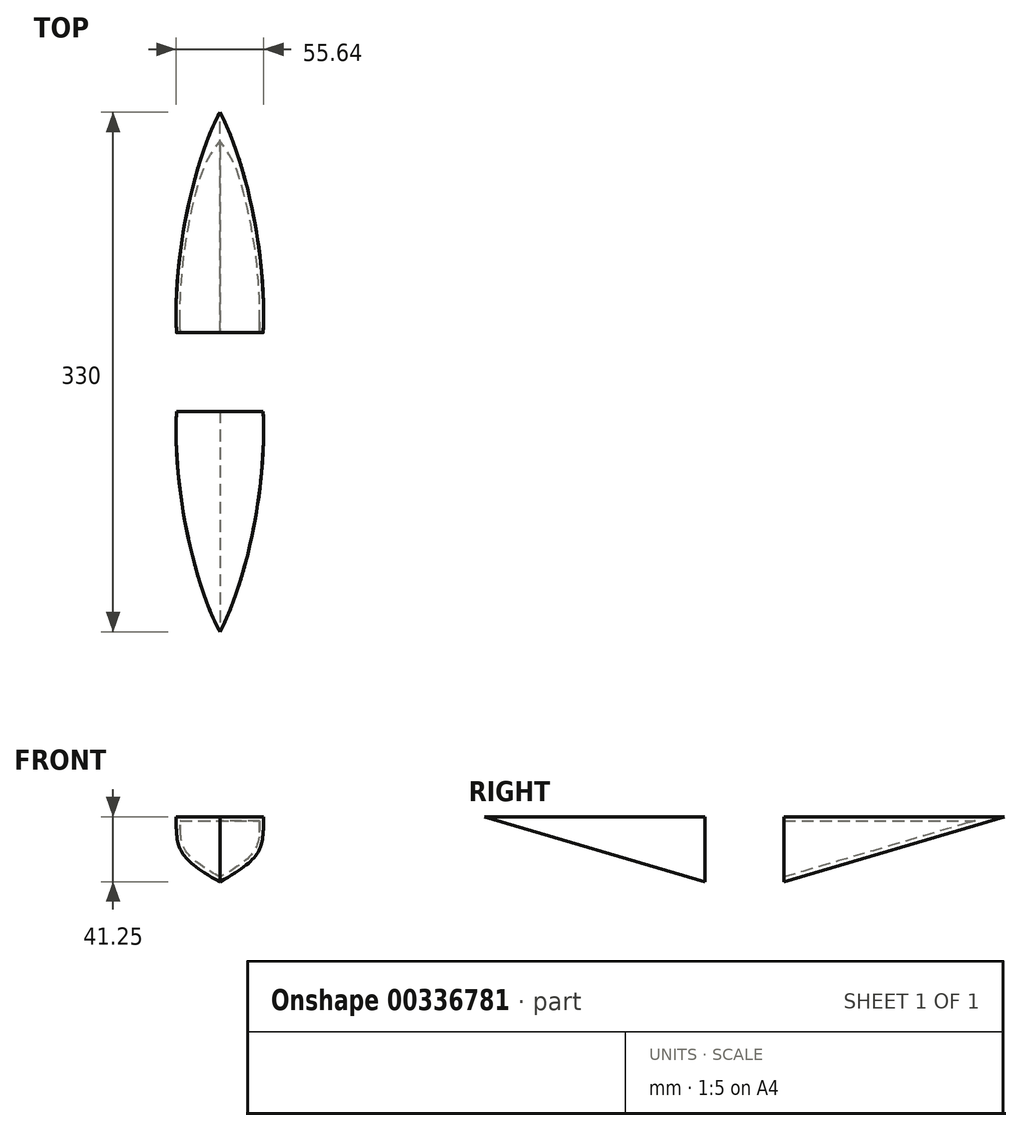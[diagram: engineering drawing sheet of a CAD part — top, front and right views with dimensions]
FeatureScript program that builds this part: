
annotation { "Feature Type Name" : "Feature", "Feature Type Description" : "" }
export const myFeature = defineFeature(function(context is Context, id is Id, definition is map)
    precondition{}
    {
        {
            var Q0;
            Q0=qCreatedBy(makeId("Front.planeOp"),FACE);
            cPlane(context, id + "F0", {"entities" : qUnion([Q0]), "cplaneType" : CPlaneType.OFFSET, "offset" : 25 * mm, "width" : 150 * mm, "height" : 150 * mm});
        }
        {
            var Q0;
            Q0=qCreatedBy(id+"F0.planeOp",FACE);
            var sketch = newSketch(context, id + "F1", { "sketchPlane" : qUnion([Q0])});
            skFitSpline(sketch, "E0", {"points": [v(-27.5, 0) * mm, v(0, -41.25) * mm], "startDerivative": vector(-0.33, -56.29) * mm, "endDerivative": vector(86.65, -47.52) * mm});
            skFitSpline(sketch, "E1.MirrorCS", {"points": [v(27.5, 0) * mm, v(0, -41.25) * mm], "startDerivative": vector(0.33, -56.29) * mm, "endDerivative": vector(-86.65, -47.52) * mm});
            skPoint(sketch, "E2.start.orphan", {"position": v(0, 0) * mm});
            skLineSegment(sketch, "E3", {"start": v(-27.5, 0) * mm, "end": v(27.5, 0) * mm});
            skSolve(sketch);
        }
        {
            var Q0;
            Q0=qCreatedBy(makeId("Top.planeOp"),FACE);
            var sketch = newSketch(context, id + "F2", { "sketchPlane" : qUnion([Q0])});
            skPoint(sketch, "E4", {"position": v(0, 115) * mm});
            skPoint(sketch, "E5.0", {"position": v(-27.5, -25) * mm});
            skPoint(sketch, "E6.0", {"position": v(27.5, -25) * mm});
            skFitSpline(sketch, "E7", {"points": [v(0, 115) * mm, v(27.5, -25) * mm], "startDerivative": vector(51.02, -94.7) * mm, "endDerivative": vector(-7.57, -139.83) * mm});
            skFitSpline(sketch, "E8.MirrorCS", {"points": [v(0, 115) * mm, v(-27.5, -25) * mm], "startDerivative": vector(-51.02, -94.7) * mm, "endDerivative": vector(7.57, -139.83) * mm});
            skSolve(sketch);
        }
        {
            var Q0;
            Q0=qCreatedBy(makeId("Right.planeOp"),FACE);
            var sketch = newSketch(context, id + "F3", { "sketchPlane" : qUnion([Q0])});
            skPoint(sketch, "E9.0", {"position": v(115, 0) * mm});
            skPoint(sketch, "E10.0", {"position": v(-25, -41.25) * mm});
            skFitSpline(sketch, "E11", {"points": [v(115, 0) * mm, v(-25, -41.25) * mm], "startDerivative": vector(-45.48, -55.52) * mm, "endDerivative": vector(-255.3, -0.79) * mm});
            skSolve(sketch);
        }
        {
            var Q0;
            Q0=makeQuery(id+"F1.imprint","IMPRINT",FACE,{"disambiguationData":[TD([[makeQuery(id+"F1.imprint","IMPRINT",EDGE,{"derivedFrom":sQuery(id+"F1.wireOp",EDGE,"E0")}),1.0]])]});
            var Q1;
            Q1=sQuery(id+"F2.wireOp",VERTEX,"E4");
            var Q2;
            Q2=sQuery(id+"F2.wireOp",EDGE,"E7");
            var Q3;
            Q3=sQuery(id+"F2.wireOp",EDGE,"E8.MirrorCS");
            loft(context, id + "F4", {"addGuides" : true, "sheetProfilesArray" : [{ "sheetProfileEntities" : qUnion([Q0]) }, { "sheetProfileEntities" : qUnion([Q1]) }], "guidesArray" : [{ "guideEntities" : qUnion([Q2]), "guideDerivativeType" : LoftGuideDerivativeType.DEFAULT, "guideDerivativeMagnitude" : 1 }, { "guideEntities" : qUnion([Q3]), "guideDerivativeType" : LoftGuideDerivativeType.DEFAULT, "guideDerivativeMagnitude" : 1 }]});
        }
        {
            var Q0;
            Q0=qCreatedBy(id+"F0.planeOp",FACE);
            cPlane(context, id + "F5", {"entities" : qUnion([Q0]), "cplaneType" : CPlaneType.OFFSET, "offset" : 25 * mm, "width" : 150 * mm, "height" : 150 * mm});
        }
        {
            var Q0;
            Q0=makeQuery(id+"F4.opLoft","SWEPT_BODY",BODY,{"disambiguationData":[OSD([makeQuery(id+"F1.imprint","IMPRINT",FACE,{"disambiguationData":[TD([[makeQuery(id+"F1.imprint","IMPRINT",EDGE,{"derivedFrom":sQuery(id+"F1.wireOp",EDGE,"E0")}),1.0]])]}),sQuery(id+"F2.wireOp",EDGE,"E7"),sQuery(id+"F2.wireOp",EDGE,"E8.MirrorCS"),sQuery(id+"F3.wireOp",VERTEX,"E9.0"),sQuery(id+"F3.wireOp",EDGE,"E11")])]});
            var Q1;
            Q1=qCreatedBy(id+"F5.planeOp",FACE);
            mirror(context, id + "F6", {"entities" : qUnion([Q0]), "mirrorPlane" : qUnion([Q1])});
        }
        {
            var Q0;
            Q0=makeQuery(id+"F4.opLoft","CAP_FACE",FACE,{"disambiguationData":[OSD([makeQuery(id+"F1.imprint","IMPRINT",FACE,{"disambiguationData":[TD([[makeQuery(id+"F1.imprint","IMPRINT",EDGE,{"derivedFrom":sQuery(id+"F1.wireOp",EDGE,"E0")}),1.0]])]})])],"isStart":true});
            shell(context, id + "F7", {"entities" : qUnion([Q0]), "thickness" : 2.5 * mm});
        }
    });
